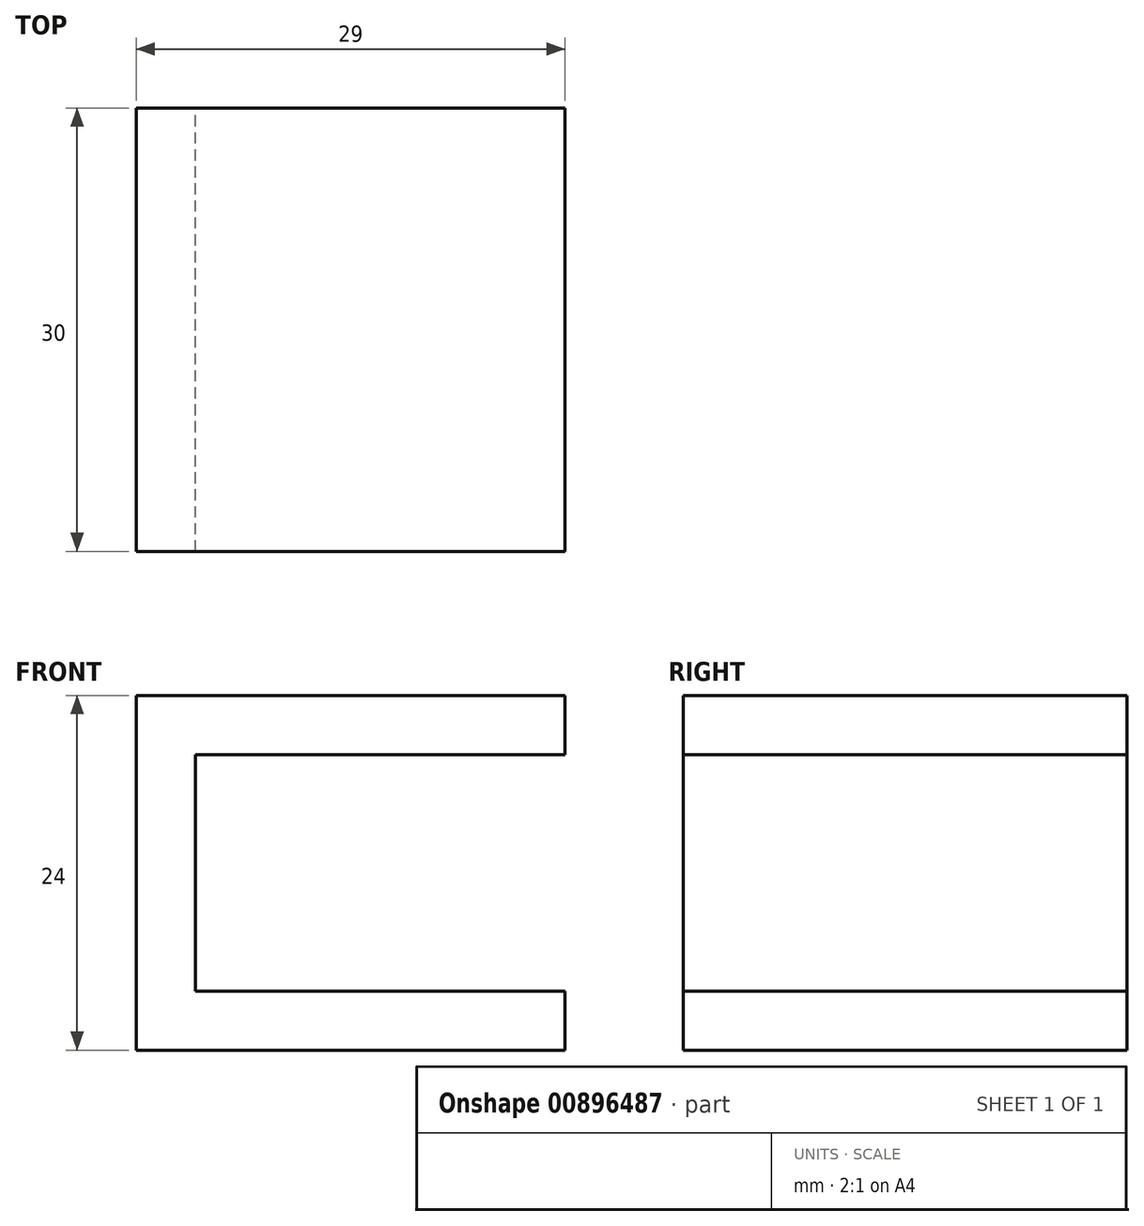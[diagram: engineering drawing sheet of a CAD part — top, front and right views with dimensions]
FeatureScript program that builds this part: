
annotation { "Feature Type Name" : "Feature", "Feature Type Description" : "" }
export const myFeature = defineFeature(function(context is Context, id is Id, definition is map)
    precondition{}
    {
        {
            var Q0;
            Q0=qCreatedBy(makeId("Front.planeOp"),FACE);
            var sketch = newSketch(context, id + "F0", { "sketchPlane" : qUnion([Q0])});
            skLineSegment(sketch, "E0.bottom", {"start": v(0, 0) * mm, "end": v(25, 0) * mm});
            skLineSegment(sketch, "E0.top", {"start": v(0, 16) * mm, "end": v(25, 16) * mm});
            skLineSegment(sketch, "E0.left", {"start": v(0, 0) * mm, "end": v(0, 16) * mm});
            skLineSegment(sketch, "E1.0", {"start": v(-4, 20) * mm, "end": v(25, 20) * mm});
            skLineSegment(sketch, "E1.1", {"start": v(-4, -4) * mm, "end": v(-4, 20) * mm});
            skLineSegment(sketch, "E1.2", {"start": v(-4, -4) * mm, "end": v(25, -4) * mm});
            skLineSegment(sketch, "E2", {"start": v(25, 20) * mm, "end": v(25, 16) * mm});
            skLineSegment(sketch, "E3", {"start": v(25, 0) * mm, "end": v(25, -4) * mm});
            skSolve(sketch);
        }
        {
            var Q0;
            Q0 = qSketchRegion(id + "F0", true);
            extrude(context, id + "F1", {"entities" : qUnion([Q0]), "depth" : 30 * mm, "offsetDistance" : 25 * mm});
        }
    });
